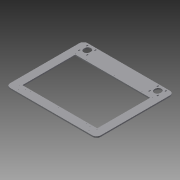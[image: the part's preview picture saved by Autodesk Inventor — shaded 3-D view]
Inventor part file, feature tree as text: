
AUTODESK INVENTOR PART (.ipt)
format: ipt  version: 2014 SP1 (Build 180222100, 222)  size: 154,624 bytes
history: native  units: in
note: dims shown in document units (in); Inventor stores cm internally (conversion verified against a paired STEP export)
features: extrude x1, sketch x1
ambient origin geometry x8: Origin, YZ Plane, XZ Plane, XY Plane, X Axis, Y Axis, Z Axis, Center Point
bodies: Solid1 (feature_tree)
feature tree (2):
  extrude  "Extrusion1"  [1 undecoded]
  sketch  "Sketch1"  dims[d0=0.1875in d1=0.0in]
note: 1 required parameter value undecoded (feature->parameter linkage not recoverable at this tier; creation-order binding heuristic only, values carry confidence <= 0.55)
